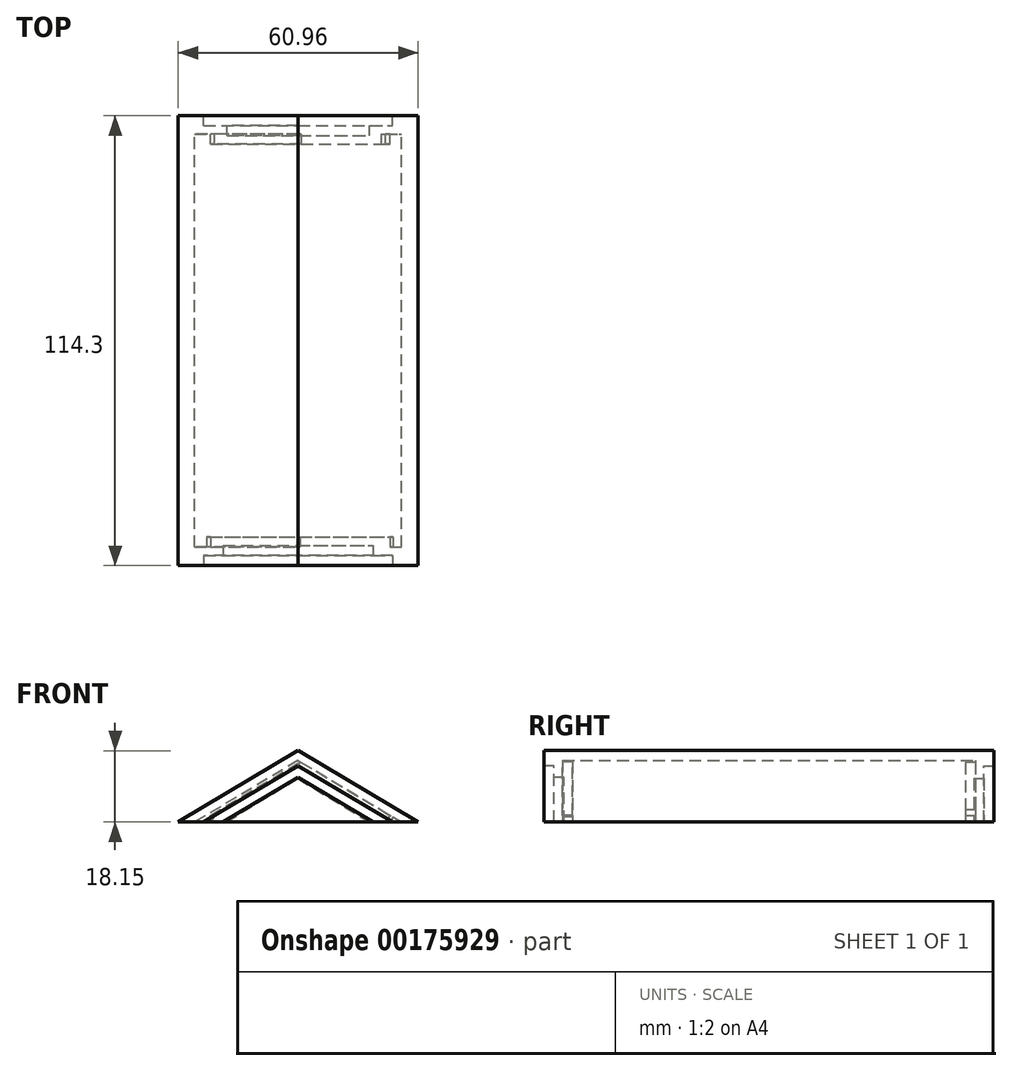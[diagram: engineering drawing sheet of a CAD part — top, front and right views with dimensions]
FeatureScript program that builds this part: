
annotation { "Feature Type Name" : "Feature", "Feature Type Description" : "" }
export const myFeature = defineFeature(function(context is Context, id is Id, definition is map)
    precondition{}
    {
        {
            var Q0;
            Q0=qCreatedBy(makeId("Front.planeOp"),FACE);
            var sketch = newSketch(context, id + "F0", { "sketchPlane" : qUnion([Q0])});
            skLineSegment(sketch, "E0", {"start": v(-30.48, 0) * mm, "end": v(30.48, 0) * mm});
            skLineSegment(sketch, "E1", {"start": v(30.48, 0) * mm, "end": v(0, 18.15) * mm});
            skLineSegment(sketch, "E2", {"start": v(0, 18.15) * mm, "end": v(-30.48, 0) * mm});
            skSolve(sketch);
        }
        {
            var Q0;
            Q0=makeQuery(id+"F0.imprint","IMPRINT",FACE,{"disambiguationData":[TD([[makeQuery(id+"F0.imprint","IMPRINT",EDGE,{"derivedFrom":sQuery(id+"F0.wireOp",EDGE,"E0")}),1.0]])]});
            extrude(context, id + "F1", {"entities" : qUnion([Q0]), "endBound" : BoundingType.SYMMETRIC, "depth" : 114.3 * mm});
        }
        {
            var Q0;
            Q0=makeQuery(id+"F1.opExtrude","CAP_FACE",FACE,{"disambiguationData":[OSD([sQuery(id+"F0.wireOp",EDGE,"E0"),sQuery(id+"F0.wireOp",EDGE,"E1"),sQuery(id+"F0.wireOp",EDGE,"E2")])],"isStart":false});
            var sketch = newSketch(context, id + "F2", { "sketchPlane" : qUnion([Q0])});
            skLineSegment(sketch, "E3", {"start": v(24.03, 0) * mm, "end": v(0, 14.3) * mm});
            skLineSegment(sketch, "E4", {"start": v(0, 14.3) * mm, "end": v(-24.03, 0) * mm});
            skLineSegment(sketch, "E5", {"start": v(-19.06, 0) * mm, "end": v(0, 11.35) * mm});
            skLineSegment(sketch, "E6", {"start": v(0, 11.35) * mm, "end": v(19.06, 0) * mm});
            skLineSegment(sketch, "E7", {"start": v(-19.06, 0) * mm, "end": v(0, 0) * mm});
            skLineSegment(sketch, "E8", {"start": v(0, 0) * mm, "end": v(19.06, 0) * mm});
            skLineSegment(sketch, "E9", {"start": v(-19.06, 0) * mm, "end": v(-24.03, 0) * mm});
            skLineSegment(sketch, "E10", {"start": v(19.06, 0) * mm, "end": v(24.03, 0) * mm});
            skSolve(sketch);
        }
        {
            var Q0;
            Q0=makeQuery(id+"F1.opExtrude","CAP_FACE",FACE,{"disambiguationData":[OSD([sQuery(id+"F0.wireOp",EDGE,"E0"),sQuery(id+"F0.wireOp",EDGE,"E1"),sQuery(id+"F0.wireOp",EDGE,"E2")])],"isStart":true});
            var sketch = newSketch(context, id + "F3", { "sketchPlane" : qUnion([Q0])});
            skLineSegment(sketch, "E11", {"start": v(0, 11.05) * mm, "end": v(-18.1, 0) * mm});
            skLineSegment(sketch, "E12", {"start": v(0, 11.05) * mm, "end": v(18.1, 0) * mm});
            skLineSegment(sketch, "E13", {"start": v(24, 0) * mm, "end": v(0, 14.34) * mm});
            skLineSegment(sketch, "E14", {"start": v(0, 14.34) * mm, "end": v(-24, 0) * mm});
            skLineSegment(sketch, "E15", {"start": v(-18.1, 0) * mm, "end": v(0, 0) * mm});
            skLineSegment(sketch, "E16", {"start": v(0, 0) * mm, "end": v(18.1, 0) * mm});
            skLineSegment(sketch, "E17", {"start": v(-24, 0) * mm, "end": v(-18.1, 0) * mm});
            skLineSegment(sketch, "E18", {"start": v(18.1, 0) * mm, "end": v(24, 0) * mm});
            skSolve(sketch);
        }
        {
            var Q0;
            Q0=makeQuery(id+"F2.imprint","IMPRINT",FACE,{"disambiguationData":[TD([[makeQuery(id+"F2.imprint","IMPRINT",EDGE,{"derivedFrom":sQuery(id+"F2.wireOp",EDGE,"E5")}),-1.0]])]});
            extrude(context, id + "F4", {"entities" : qUnion([Q0]), "operationType" : NewBodyOperationType.REMOVE, "oppositeDirection" : true, "depth" : 5.08 * mm});
        }
        {
            var Q0;
            Q0=makeQuery(id+"F2.imprint","IMPRINT",FACE,{"disambiguationData":[TD([[makeQuery(id+"F2.imprint","IMPRINT",EDGE,{"derivedFrom":sQuery(id+"F2.wireOp",EDGE,"E3")}),1.0]])]});
            extrude(context, id + "F5", {"entities" : qUnion([Q0]), "operationType" : NewBodyOperationType.REMOVE, "oppositeDirection" : true, "depth" : 2.54 * mm});
        }
        {
            var Q0;
            Q0=makeQuery(id+"F3.imprint","IMPRINT",FACE,{"disambiguationData":[TD([[makeQuery(id+"F3.imprint","IMPRINT",EDGE,{"derivedFrom":sQuery(id+"F3.wireOp",EDGE,"E11")}),1.0]])]});
            extrude(context, id + "F6", {"entities" : qUnion([Q0]), "operationType" : NewBodyOperationType.REMOVE, "oppositeDirection" : true, "depth" : 5.08 * mm});
        }
        {
            var Q0;
            Q0=makeQuery(id+"F3.imprint","IMPRINT",FACE,{"disambiguationData":[TD([[makeQuery(id+"F3.imprint","IMPRINT",EDGE,{"derivedFrom":sQuery(id+"F3.wireOp",EDGE,"E11")}),-1.0]])]});
            extrude(context, id + "F7", {"entities" : qUnion([Q0]), "operationType" : NewBodyOperationType.REMOVE, "oppositeDirection" : true, "depth" : 2.54 * mm});
        }
        {
            var Q0;
            Q0=makeQuery(id+"F1.opExtrude","SWEPT_FACE",FACE,{"disambiguationData":[OSD([sQuery(id+"F0.wireOp",EDGE,"E0")])]});
            shell(context, id + "F8", {"entities" : qUnion([Q0]), "thickness" : 2.16 * mm});
        }
        {
            var Q0;
            Q0=makeQuery(id+"F8.opShell","OFFSET_FACE",FACE,{"disambiguationData":[OSD([sQuery(id+"F2.wireOp",EDGE,"E6")])]});
            var Q1;
            Q1=makeQuery(id+"F8.opShell","OFFSET_FACE",FACE,{"disambiguationData":[OSD([sQuery(id+"F2.wireOp",EDGE,"E5")])]});
            var Q2;
            Q2=makeQuery(id+"F8.opShell","OFFSET_FACE",FACE,{"disambiguationData":[OSD([sQuery(id+"F3.wireOp",EDGE,"E12")])]});
            var Q3;
            Q3=makeQuery(id+"F8.opShell","OFFSET_FACE",FACE,{"disambiguationData":[OSD([sQuery(id+"F3.wireOp",EDGE,"E11")])]});
            extrude(context, id + "F9", {"entities" : qUnion([Q0, Q1, Q2, Q3]), "operationType" : NewBodyOperationType.ADD, "depth" : 2.03 * mm});
        }
    });
